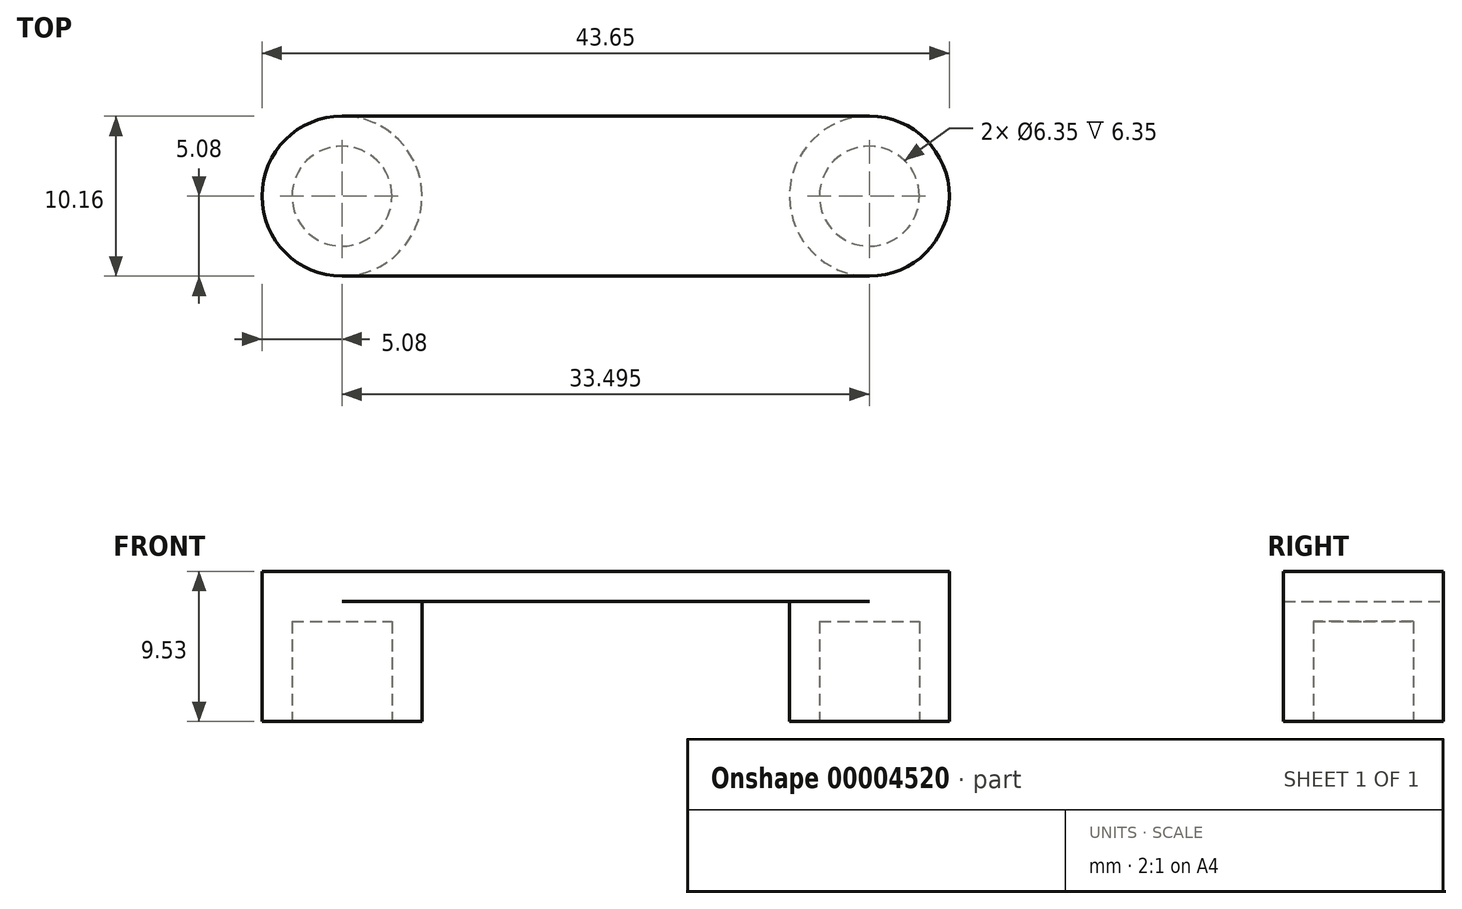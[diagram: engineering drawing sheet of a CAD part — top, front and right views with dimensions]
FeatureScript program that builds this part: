
annotation { "Feature Type Name" : "Feature", "Feature Type Description" : "" }
export const myFeature = defineFeature(function(context is Context, id is Id, definition is map)
    precondition{}
    {
        {
            var Q0;
            Q0=qCreatedBy(makeId("Top.planeOp"),FACE);
            var sketch = newSketch(context, id + "F0", { "sketchPlane" : qUnion([Q0])});
            skLineSegment(sketch, "E0.bottom", {"start": v(5.08, 0) * mm, "end": v(38.57, 0) * mm});
            skLineSegment(sketch, "E0.top", {"start": v(5.08, 10.16) * mm, "end": v(38.57, 10.16) * mm});
            skArc(sketch, "E1", {"start": v(5.08, 10.16) * mm, "mid": v(0, 5.08) * mm, "end": v(5.08, 0) * mm});
            skLineSegment(sketch, "E2", {"start": v(21.83, 10.16) * mm, "end": v(21.83, 0) * mm, "construction": true});
            skArc(sketch, "E3.0.MirrorCS", {"start": v(38.57, 10.16) * mm, "mid": v(43.65, 5.08) * mm, "end": v(38.57, 0) * mm});
            skPoint(sketch, "E4.orphan", {"position": v(43.65, 0) * mm});
            skPoint(sketch, "E5.orphan", {"position": v(46, 10.16) * mm});
            skPoint(sketch, "E6.orphan", {"position": v(-2.35, 10.16) * mm});
            skPoint(sketch, "E7.orphan", {"position": v(0, 0) * mm});
            skSolve(sketch);
        }
        {
            var Q0;
            Q0 = qSketchRegion(id + "F0", true);
            extrude(context, id + "F1", {"entities" : qUnion([Q0]), "depth" : 1.9 * mm});
        }
        {
            var Q0;
            Q0=makeQuery(id+"F1.opExtrude","CAP_FACE",FACE,{"disambiguationData":[OSD([sQuery(id+"F0.wireOp",EDGE,"E0.bottom"),sQuery(id+"F0.wireOp",EDGE,"E0.top"),sQuery(id+"F0.wireOp",EDGE,"E1"),sQuery(id+"F0.wireOp",EDGE,"E3.0.MirrorCS")])],"isStart":true});
            var sketch = newSketch(context, id + "F2", { "sketchPlane" : qUnion([Q0])});
            skCircle(sketch, "E8", {"center": v(5.08, -5.08) * mm, "radius": 5.08 * mm});
            skCircle(sketch, "E9", {"center": v(38.57, -5.08) * mm, "radius": 5.08 * mm});
            skSolve(sketch);
        }
        {
            var Q0;
            Q0 = qSketchRegion(id + "F2", true);
            extrude(context, id + "F3", {"entities" : qUnion([Q0]), "operationType" : NewBodyOperationType.ADD, "depth" : 7.62 * mm});
        }
        {
            var Q0;
            Q0=makeQuery(id+"F3.opExtrude","CAP_FACE",FACE,{"disambiguationData":[OSD([sQuery(id+"F2.wireOp",EDGE,"E8")])],"isStart":false});
            var sketch = newSketch(context, id + "F4", { "sketchPlane" : qUnion([Q0])});
            skCircle(sketch, "E10", {"center": v(5.08, -5.08) * mm, "radius": 3.18 * mm});
            skSolve(sketch);
        }
        {
            var Q0;
            Q0 = qSketchRegion(id + "F4", true);
            extrude(context, id + "F5", {"entities" : qUnion([Q0]), "operationType" : NewBodyOperationType.REMOVE, "oppositeDirection" : true, "depth" : 6.35 * mm});
        }
        {
            var Q0;
            Q0=makeQuery(id+"F3.opExtrude","CAP_FACE",FACE,{"disambiguationData":[OSD([sQuery(id+"F2.wireOp",EDGE,"E9")])],"isStart":false});
            var sketch = newSketch(context, id + "F6", { "sketchPlane" : qUnion([Q0])});
            skCircle(sketch, "E11", {"center": v(38.57, -5.08) * mm, "radius": 3.18 * mm});
            skSolve(sketch);
        }
        {
            var Q0;
            Q0 = qSketchRegion(id + "F6", true);
            extrude(context, id + "F7", {"entities" : qUnion([Q0]), "operationType" : NewBodyOperationType.REMOVE, "oppositeDirection" : true, "depth" : 6.35 * mm});
        }
    });
